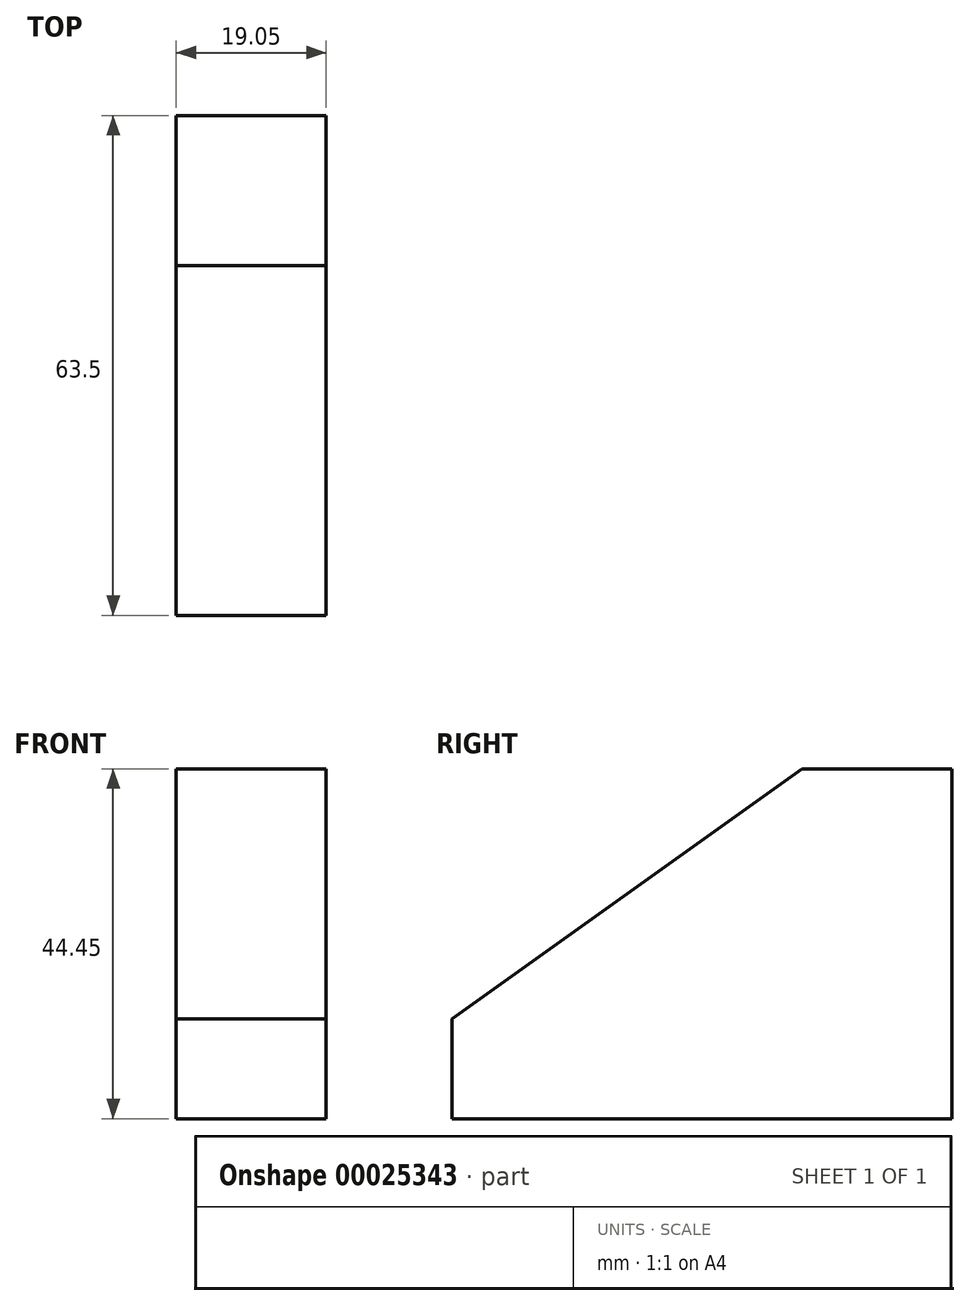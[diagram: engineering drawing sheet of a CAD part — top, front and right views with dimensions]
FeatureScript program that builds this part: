
annotation { "Feature Type Name" : "Feature", "Feature Type Description" : "" }
export const myFeature = defineFeature(function(context is Context, id is Id, definition is map)
    precondition{}
    {
        {
            var Q0;
            Q0=qCreatedBy(makeId("Right.planeOp"),FACE);
            var sketch = newSketch(context, id + "F0", { "sketchPlane" : qUnion([Q0])});
            skLineSegment(sketch, "E0", {"start": v(-37.02, -36.27) * mm, "end": v(26.48, -36.27) * mm});
            skLineSegment(sketch, "E1", {"start": v(26.48, -36.27) * mm, "end": v(26.48, 8.18) * mm});
            skLineSegment(sketch, "E2", {"start": v(26.48, 8.18) * mm, "end": v(7.43, 8.18) * mm});
            skLineSegment(sketch, "E3", {"start": v(-37.02, -36.27) * mm, "end": v(-37.02, -23.57) * mm});
            skLineSegment(sketch, "E4", {"start": v(-37.02, -23.57) * mm, "end": v(7.43, 8.18) * mm});
            skSolve(sketch);
        }
        {
            var Q0;
            Q0=makeQuery(id+"F0.imprint","IMPRINT",FACE,{"disambiguationData":[TD([[makeQuery(id+"F0.imprint","IMPRINT",EDGE,{"derivedFrom":sQuery(id+"F0.wireOp",EDGE,"E0")}),1.0]])]});
            extrude(context, id + "F1", {"entities" : qUnion([Q0]), "depth" : 19.05 * mm});
        }
    });
